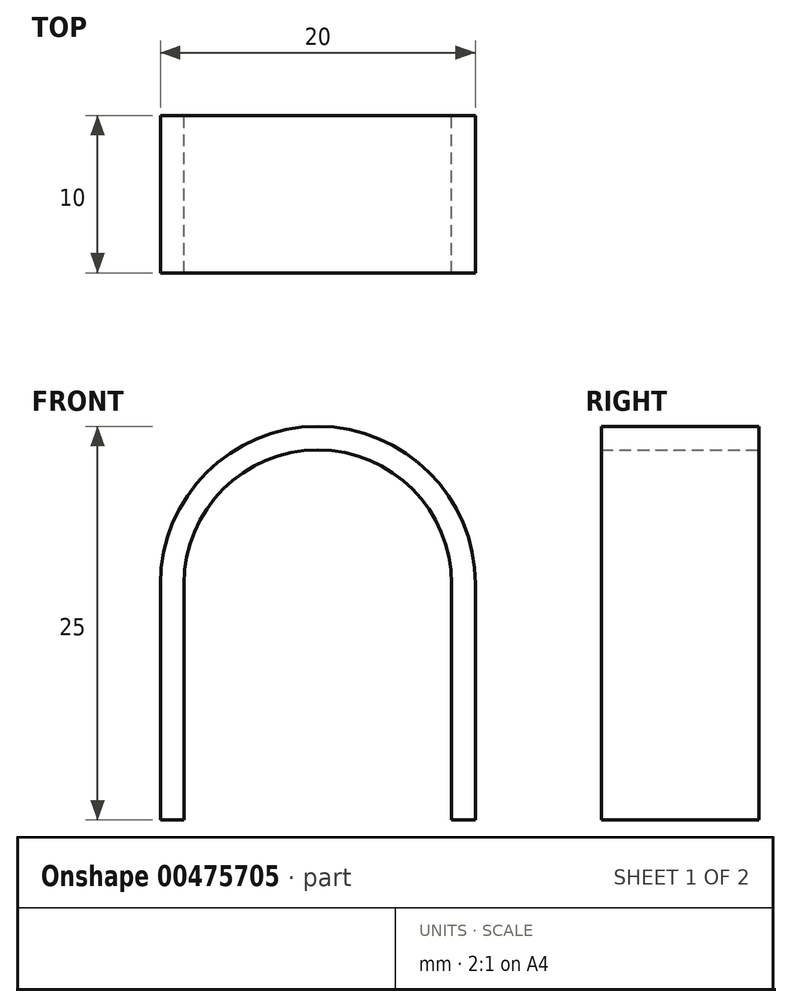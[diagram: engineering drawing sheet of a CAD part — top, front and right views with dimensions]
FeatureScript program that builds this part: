
annotation { "Feature Type Name" : "Feature", "Feature Type Description" : "" }
export const myFeature = defineFeature(function(context is Context, id is Id, definition is map)
    precondition{}
    {
        {
            var Q0;
            Q0=qCreatedBy(makeId("Front.planeOp"),FACE);
            var sketch = newSketch(context, id + "F0", { "sketchPlane" : qUnion([Q0])});
            skArc(sketch, "E0", {"start": v(10, 0) * mm, "mid": v(0, 10) * mm, "end": v(-10, 0) * mm});
            skArc(sketch, "E1", {"start": v(8.5, 0) * mm, "mid": v(0, 8.5) * mm, "end": v(-8.5, 0) * mm});
            skLineSegment(sketch, "E2", {"start": v(10, 0) * mm, "end": v(10, -10) * mm});
            skLineSegment(sketch, "E3", {"start": v(8.5, -10) * mm, "end": v(10, -10) * mm});
            skLineSegment(sketch, "E4", {"start": v(-8.5, -10) * mm, "end": v(-10, -10) * mm});
            skPoint(sketch, "E5.end.orphan", {"position": v(-10, -9.44) * mm});
            skPoint(sketch, "E5.start.orphan", {"position": v(-10, 0) * mm});
            skLineSegment(sketch, "E6", {"start": v(-10, 0) * mm, "end": v(-10, -10) * mm});
            skLineSegment(sketch, "E7", {"start": v(-8.5, 0) * mm, "end": v(-8.5, -10) * mm});
            skLineSegment(sketch, "E8", {"start": v(8.5, 0) * mm, "end": v(8.5, -10) * mm});
            skPoint(sketch, "E9.orphan", {"position": v(0, -10) * mm});
            skLineSegment(sketch, "E10", {"start": v(-10, -10) * mm, "end": v(-10, -15) * mm});
            skLineSegment(sketch, "E11", {"start": v(-10, -15) * mm, "end": v(-8.5, -15) * mm});
            skLineSegment(sketch, "E12", {"start": v(-8.5, -15) * mm, "end": v(-8.5, -10) * mm});
            skLineSegment(sketch, "E13", {"start": v(10, -10) * mm, "end": v(10, -15) * mm});
            skLineSegment(sketch, "E14", {"start": v(8.5, -10) * mm, "end": v(8.5, -15) * mm});
            skLineSegment(sketch, "E15", {"start": v(8.5, -15) * mm, "end": v(10, -15) * mm});
            skSolve(sketch);
        }
        {
            var Q0;
            Q0 = qSketchRegion(id + "F0", true);
            extrude(context, id + "F1", {"entities" : qUnion([Q0]), "depth" : 10 * mm, "offsetDistance" : 25 * mm});
        }
    });
